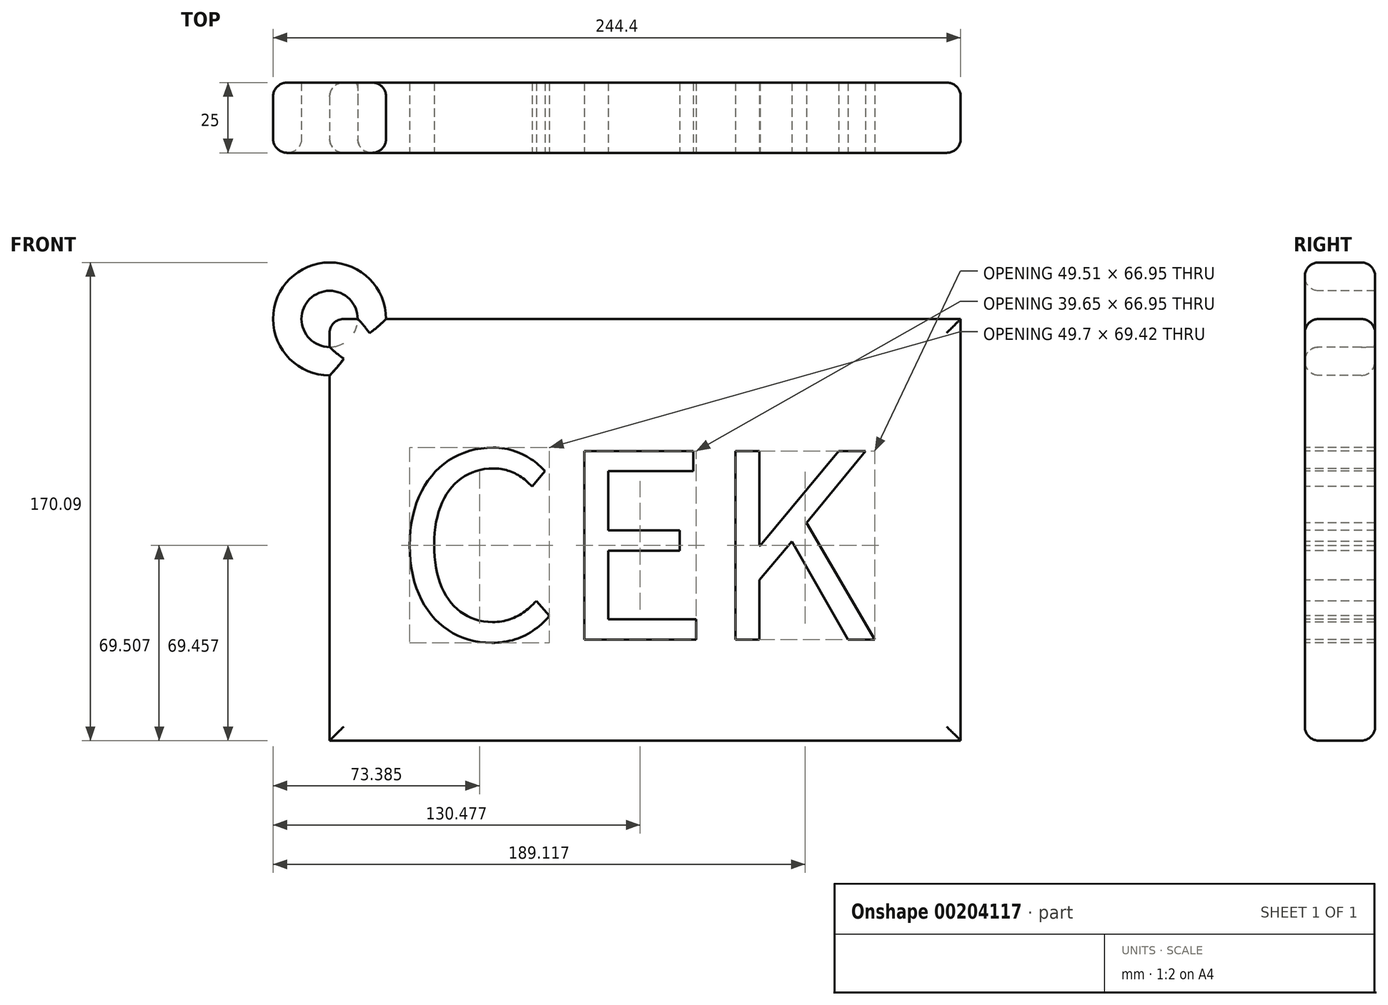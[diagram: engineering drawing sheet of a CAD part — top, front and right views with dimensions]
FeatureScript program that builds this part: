
annotation { "Feature Type Name" : "Feature", "Feature Type Description" : "" }
export const myFeature = defineFeature(function(context is Context, id is Id, definition is map)
    precondition{}
    {
        {
            var Q0;
            Q0=qCreatedBy(makeId("Front.planeOp"),FACE);
            var sketch = newSketch(context, id + "F0", { "sketchPlane" : qUnion([Q0])});
            skLineSegment(sketch, "E0.0", {"start": v(-110.9, -75) * mm, "end": v(113.42, -75) * mm});
            skLineSegment(sketch, "E1.0", {"start": v(-110.9, 75) * mm, "end": v(113.42, 75) * mm});
            skLineSegment(sketch, "E2", {"start": v(-110.9, 75) * mm, "end": v(-110.9, -75) * mm});
            skLineSegment(sketch, "E3", {"start": v(113.42, 75) * mm, "end": v(113.42, -75) * mm});
            skText(sketch, "E4", { "text": "CEK\n", "fontName": "NotoSansCJKsc-Regular.otf"});
            const initialGuessF0  = {"E4": [-0.08774, -0.03902, 1, 0, 0.06577]};
            skSetInitialGuess(sketch, initialGuessF0);
            skSolve(sketch);
        }
        {
            var Q0;
            Q0=makeQuery(id+"F0.imprint","IMPRINT",FACE,{"disambiguationData":[TD([[makeQuery(id+"F0.imprint","IMPRINT",EDGE,{"derivedFrom":sQuery(id+"F0.wireOp",EDGE,"E0.0")}),1.0]])]});
            extrude(context, id + "F1", {"entities" : qUnion([Q0]), "oppositeDirection" : true, "depth" : 25 * mm});
        }
        {
            var Q0;
            Q0=makeQuery(id+"F1.opExtrude","CAP_FACE",FACE,{"disambiguationData":[OSD([sQuery(id+"F0.wireOp",EDGE,"E0.0"),sQuery(id+"F0.wireOp",EDGE,"E1.0"),sQuery(id+"F0.wireOp",EDGE,"E2"),sQuery(id+"F0.wireOp",EDGE,"E3"),sQuery(id+"F0.wireOp",EDGE,"E4.sketch_text.stroke-0"),sQuery(id+"F0.wireOp",EDGE,"E4.sketch_text.stroke-1"),sQuery(id+"F0.wireOp",EDGE,"E4.sketch_text.stroke-2"),sQuery(id+"F0.wireOp",EDGE,"E4.sketch_text.stroke-3"),sQuery(id+"F0.wireOp",EDGE,"E4.sketch_text.stroke-4"),sQuery(id+"F0.wireOp",EDGE,"E4.sketch_text.stroke-5"),sQuery(id+"F0.wireOp",EDGE,"E4.sketch_text.stroke-6"),sQuery(id+"F0.wireOp",EDGE,"E4.sketch_text.stroke-7"),sQuery(id+"F0.wireOp",EDGE,"E4.sketch_text.stroke-8"),sQuery(id+"F0.wireOp",EDGE,"E4.sketch_text.stroke-9"),sQuery(id+"F0.wireOp",EDGE,"E4.sketch_text.stroke-10"),sQuery(id+"F0.wireOp",EDGE,"E4.sketch_text.stroke-11"),sQuery(id+"F0.wireOp",EDGE,"E4.sketch_text.stroke-12"),sQuery(id+"F0.wireOp",EDGE,"E4.sketch_text.stroke-13"),sQuery(id+"F0.wireOp",EDGE,"E4.sketch_text.stroke-14"),sQuery(id+"F0.wireOp",EDGE,"E4.sketch_text.stroke-15"),sQuery(id+"F0.wireOp",EDGE,"E4.sketch_text.stroke-16"),sQuery(id+"F0.wireOp",EDGE,"E4.sketch_text.stroke-17"),sQuery(id+"F0.wireOp",EDGE,"E4.sketch_text.stroke-18"),sQuery(id+"F0.wireOp",EDGE,"E4.sketch_text.stroke-19"),sQuery(id+"F0.wireOp",EDGE,"E4.sketch_text.stroke-20"),sQuery(id+"F0.wireOp",EDGE,"E4.sketch_text.stroke-21"),sQuery(id+"F0.wireOp",EDGE,"E4.sketch_text.stroke-22"),sQuery(id+"F0.wireOp",EDGE,"E4.sketch_text.stroke-23"),sQuery(id+"F0.wireOp",EDGE,"E4.sketch_text.stroke-24"),sQuery(id+"F0.wireOp",EDGE,"E4.sketch_text.stroke-25"),sQuery(id+"F0.wireOp",EDGE,"E4.sketch_text.stroke-26"),sQuery(id+"F0.wireOp",EDGE,"E4.sketch_text.stroke-27"),sQuery(id+"F0.wireOp",EDGE,"E4.sketch_text.stroke-28"),sQuery(id+"F0.wireOp",EDGE,"E4.sketch_text.stroke-29"),sQuery(id+"F0.wireOp",EDGE,"E4.sketch_text.stroke-30"),sQuery(id+"F0.wireOp",EDGE,"E4.sketch_text.stroke-31"),sQuery(id+"F0.wireOp",EDGE,"E4.sketch_text.stroke-32"),sQuery(id+"F0.wireOp",EDGE,"E4.sketch_text.stroke-33"),sQuery(id+"F0.wireOp",EDGE,"E4.sketch_text.stroke-34")])],"isStart":true});
            var sketch = newSketch(context, id + "F2", { "sketchPlane" : qUnion([Q0])});
            skCircle(sketch, "E5", {"center": v(-110.9, 75) * mm, "radius": 20.09 * mm});
            skCircle(sketch, "E6", {"center": v(-110.9, 75) * mm, "radius": 10 * mm});
            skSolve(sketch);
        }
        {
            var Q0;
            {var subQ0=sQuery(id+"F2.wireOp",EDGE,"E5");var subQ1=makeQuery(id+"F1.opExtrude","CAP_EDGE",EDGE,{"disambiguationData":[OSD([sQuery(id+"F0.wireOp",EDGE,"E1.0")])],"isStart":true});var subQ2=makeQuery(id+"F2.imprint","INTERSECT",VERTEX,{"derivedFrom":[subQ1,subQ0]});Q0=makeQuery(id+"F2.imprint","IMPRINT",FACE,{"disambiguationData":[TD([[makeQuery(id+"F2.imprint","IMPRINT",EDGE,{"disambiguationData":[TD([[subQ2,1.0]])],"derivedFrom":subQ0}),1.0]])]});}
            extrude(context, id + "F3", {"entities" : qUnion([Q0]), "operationType" : NewBodyOperationType.ADD, "oppositeDirection" : true, "depth" : 25 * mm});
        }
        {
            var Q0;
            Q0 = qSketchRegion(id + "F2", true);
            extrude(context, id + "F4", {"entities" : qUnion([Q0]), "operationType" : NewBodyOperationType.ADD, "oppositeDirection" : true, "depth" : 25 * mm});
        }
        {
            var Q0;
            {var subQ1=sQuery(id+"F0.wireOp",EDGE,"E3");var subQ2=sQuery(id+"F0.wireOp",EDGE,"E1.0");Q0=makeQuery(id+"F4.boolean.opBoolean","SPLIT",EDGE,{"disambiguationData":[TD([makeQuery(id+"F1.opExtrude","SWEPT_FACE",FACE,{"disambiguationData":[OSD([subQ1])]})])],"derivedFrom":makeQuery(id+"F1.opExtrude","CAP_EDGE",EDGE,{"disambiguationData":[OSD([subQ2])],"isStart":true})});}
            var Q1;
            Q1=makeQuery(id+"F1.opExtrude","CAP_EDGE",EDGE,{"disambiguationData":[OSD([sQuery(id+"F0.wireOp",EDGE,"E3")])],"isStart":true});
            var Q2;
            Q2=makeQuery(id+"F1.opExtrude","CAP_EDGE",EDGE,{"disambiguationData":[OSD([sQuery(id+"F0.wireOp",EDGE,"E0.0")])],"isStart":true});
            var Q3;
            {var subQ1=sQuery(id+"F0.wireOp",EDGE,"E2");var subQ2=sQuery(id+"F0.wireOp",EDGE,"E0.0");Q3=makeQuery(id+"F4.boolean.opBoolean","SPLIT",EDGE,{"disambiguationData":[TD([makeQuery(id+"F1.opExtrude","SWEPT_FACE",FACE,{"disambiguationData":[OSD([subQ2])]})])],"derivedFrom":makeQuery(id+"F1.opExtrude","CAP_EDGE",EDGE,{"disambiguationData":[OSD([subQ1])],"isStart":true})});}
            var Q4;
            Q4=makeQuery(id+"F1.opExtrude","CAP_EDGE",EDGE,{"disambiguationData":[OSD([sQuery(id+"F0.wireOp",EDGE,"E3")])],"isStart":false});
            var Q5;
            {var subQ1=sQuery(id+"F0.wireOp",EDGE,"E3");var subQ2=sQuery(id+"F0.wireOp",EDGE,"E1.0");Q5=makeQuery(id+"F4.boolean.opBoolean","SPLIT",EDGE,{"disambiguationData":[TD([makeQuery(id+"F1.opExtrude","SWEPT_FACE",FACE,{"disambiguationData":[OSD([subQ1])]})])],"derivedFrom":makeQuery(id+"F1.opExtrude","CAP_EDGE",EDGE,{"disambiguationData":[OSD([subQ2])],"isStart":false})});}
            var Q6;
            Q6=makeQuery(id+"F1.opExtrude","CAP_EDGE",EDGE,{"disambiguationData":[OSD([sQuery(id+"F0.wireOp",EDGE,"E0.0")])],"isStart":false});
            var Q7;
            Q7=makeQuery(id+"F4.opExtrude","CAP_EDGE",EDGE,{"disambiguationData":[OSD([sQuery(id+"F2.wireOp",EDGE,"E5")])],"isStart":true});
            var Q8;
            Q8=makeQuery(id+"F4.opExtrude","CAP_EDGE",EDGE,{"disambiguationData":[OSD([sQuery(id+"F2.wireOp",EDGE,"E5")])],"isStart":false});
            var Q9;
            {var subQ1=sQuery(id+"F0.wireOp",EDGE,"E2");var subQ2=sQuery(id+"F0.wireOp",EDGE,"E0.0");Q9=makeQuery(id+"F4.boolean.opBoolean","SPLIT",EDGE,{"disambiguationData":[TD([makeQuery(id+"F1.opExtrude","SWEPT_FACE",FACE,{"disambiguationData":[OSD([subQ2])]})])],"derivedFrom":makeQuery(id+"F1.opExtrude","CAP_EDGE",EDGE,{"disambiguationData":[OSD([subQ1])],"isStart":false})});}
            var Q10;
            {var subQ1=sQuery(id+"F0.wireOp",EDGE,"E2");var subQ2=sQuery(id+"F0.wireOp",EDGE,"E1.0");Q10=makeQuery(id+"F4.boolean.opBoolean","SPLIT",EDGE,{"disambiguationData":[TD([makeQuery(id+"F1.opExtrude","SWEPT_FACE",FACE,{"disambiguationData":[OSD([subQ2])]})])],"derivedFrom":makeQuery(id+"F1.opExtrude","CAP_EDGE",EDGE,{"disambiguationData":[OSD([subQ1])],"isStart":true})});}
            var Q11;
            Q11=makeQuery(id+"F4.opExtrude","CAP_EDGE",EDGE,{"disambiguationData":[OSD([sQuery(id+"F2.wireOp",EDGE,"E6")])],"isStart":true});
            var Q12;
            {var subQ1=sQuery(id+"F0.wireOp",EDGE,"E2");var subQ2=sQuery(id+"F0.wireOp",EDGE,"E1.0");Q12=makeQuery(id+"F4.boolean.opBoolean","SPLIT",EDGE,{"disambiguationData":[TD([makeQuery(id+"F1.opExtrude","SWEPT_FACE",FACE,{"disambiguationData":[OSD([subQ1])]})])],"derivedFrom":makeQuery(id+"F1.opExtrude","CAP_EDGE",EDGE,{"disambiguationData":[OSD([subQ2])],"isStart":true})});}
            var Q13;
            {var subQ0=sQuery(id+"F0.wireOp",EDGE,"E2");var subQ2=sQuery(id+"F0.wireOp",EDGE,"E1.0");Q13=makeQuery(id+"F4.boolean.opBoolean","SPLIT",EDGE,{"disambiguationData":[TD([makeQuery(id+"F1.opExtrude","SWEPT_FACE",FACE,{"disambiguationData":[OSD([subQ2])]})])],"derivedFrom":makeQuery(id+"F1.opExtrude","CAP_EDGE",EDGE,{"disambiguationData":[OSD([subQ0])],"isStart":false})});}
            var Q14;
            {var subQ0=sQuery(id+"F0.wireOp",EDGE,"E2");var subQ2=sQuery(id+"F0.wireOp",EDGE,"E1.0");Q14=makeQuery(id+"F4.boolean.opBoolean","SPLIT",EDGE,{"disambiguationData":[TD([makeQuery(id+"F1.opExtrude","SWEPT_FACE",FACE,{"disambiguationData":[OSD([subQ0])]})])],"derivedFrom":makeQuery(id+"F1.opExtrude","CAP_EDGE",EDGE,{"disambiguationData":[OSD([subQ2])],"isStart":false})});}
            var Q15;
            Q15=makeQuery(id+"F1.opExtrude","SWEPT_EDGE",EDGE,{"disambiguationData":[OSD([sQuery(id+"F0.wireOp",EDGE,"E1.0"),sQuery(id+"F0.wireOp",EDGE,"E2")])]});
            fillet(context, id + "F5", {"entities" : qUnion([Q0, Q1, Q2, Q3, Q4, Q5, Q6, Q7, Q8, Q9, Q10, Q11, Q12, Q13, Q14, Q15]), "radius" : 5 * mm, "tangentPropagation" : true, "allowEdgeOverflow" : false});
        }
    });
